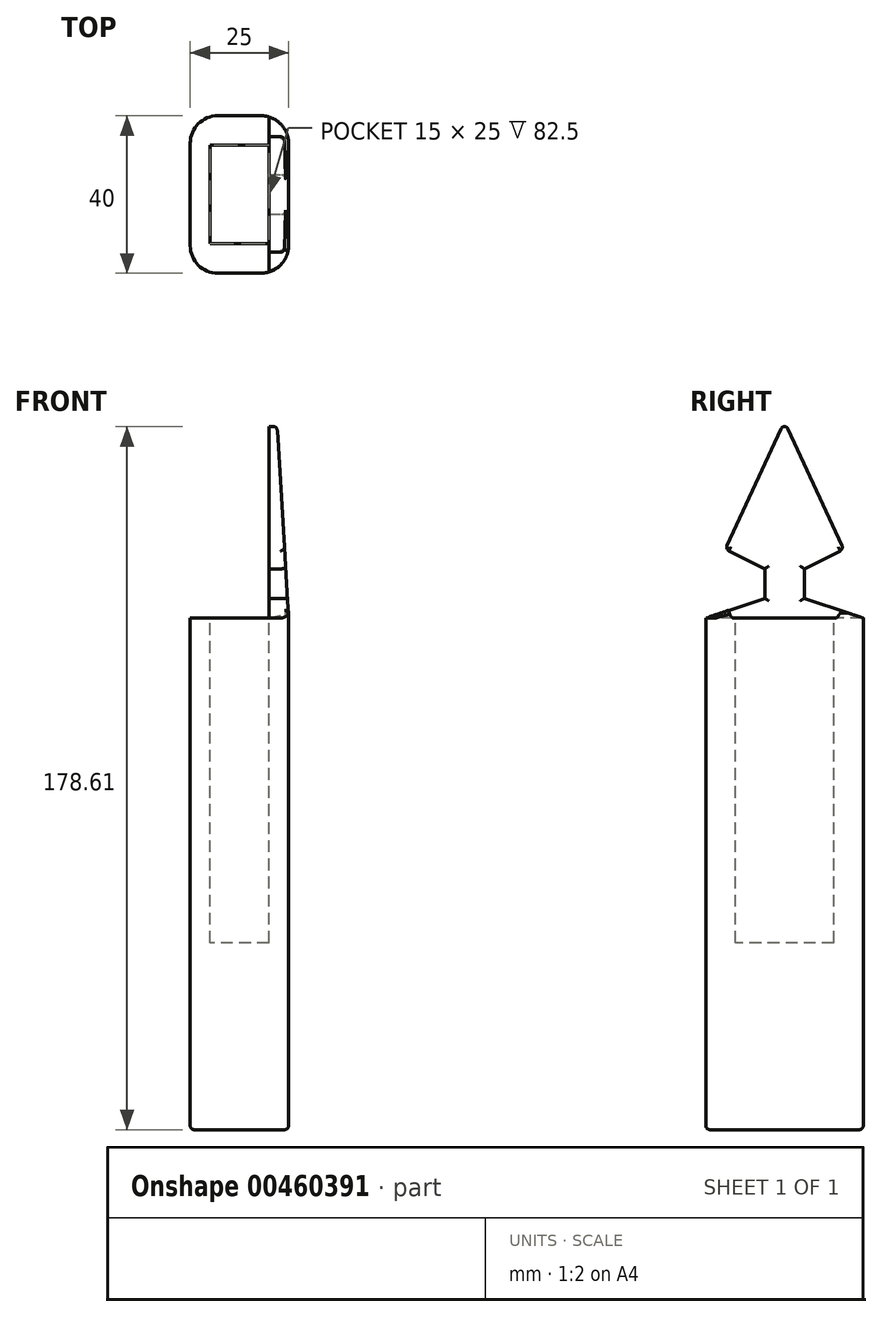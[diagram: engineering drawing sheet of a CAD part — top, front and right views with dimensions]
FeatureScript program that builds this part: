
annotation { "Feature Type Name" : "Feature", "Feature Type Description" : "" }
export const myFeature = defineFeature(function(context is Context, id is Id, definition is map)
    precondition{}
    {
        {
            var Q0;
            Q0=qCreatedBy(makeId("Top.planeOp"),FACE);
            var sketch = newSketch(context, id + "F0", { "sketchPlane" : qUnion([Q0])});
            skLineSegment(sketch, "E0.bottom", {"start": v(12.5, 20) * mm, "end": v(-12.5, 20) * mm});
            skLineSegment(sketch, "E0.top", {"start": v(12.5, -20) * mm, "end": v(-12.5, -20) * mm});
            skLineSegment(sketch, "E0.left", {"start": v(12.5, 20) * mm, "end": v(12.5, -20) * mm});
            skLineSegment(sketch, "E0.right", {"start": v(-12.5, 20) * mm, "end": v(-12.5, -20) * mm});
            skPoint(sketch, "E0.middle", {"position": v(0, 0) * mm});
            skSolve(sketch);
        }
        {
            var Q0;
            Q0=makeQuery(id+"F0.imprint","IMPRINT",FACE,{"disambiguationData":[TD([[makeQuery(id+"F0.imprint","IMPRINT",EDGE,{"derivedFrom":sQuery(id+"F0.wireOp",EDGE,"E0.bottom")}),1.0]])]});
            extrude(context, id + "F1", {"entities" : qUnion([Q0]), "endBound" : BoundingType.SYMMETRIC, "depth" : 130 * mm});
        }
        {
            var Q0;
            Q0=makeQuery(id+"F1.opExtrude","CAP_FACE",FACE,{"disambiguationData":[OSD([sQuery(id+"F0.wireOp",EDGE,"E0.bottom"),sQuery(id+"F0.wireOp",EDGE,"E0.top"),sQuery(id+"F0.wireOp",EDGE,"E0.left"),sQuery(id+"F0.wireOp",EDGE,"E0.right")])],"isStart":false});
            var sketch = newSketch(context, id + "F2", { "sketchPlane" : qUnion([Q0])});
            skLineSegment(sketch, "E1.bottom", {"start": v(7.5, 12.5) * mm, "end": v(-7.5, 12.5) * mm});
            skLineSegment(sketch, "E1.top", {"start": v(7.5, -12.5) * mm, "end": v(-7.5, -12.5) * mm});
            skLineSegment(sketch, "E1.left", {"start": v(7.5, 12.5) * mm, "end": v(7.5, -12.5) * mm});
            skLineSegment(sketch, "E1.right", {"start": v(-7.5, 12.5) * mm, "end": v(-7.5, -12.5) * mm});
            skPoint(sketch, "E1.middle", {"position": v(0, 0) * mm});
            skSolve(sketch);
        }
        {
            var Q0;
            Q0=makeQuery(id+"F2.imprint","IMPRINT",FACE,{"disambiguationData":[TD([[makeQuery(id+"F2.imprint","IMPRINT",EDGE,{"derivedFrom":sQuery(id+"F2.wireOp",EDGE,"35c8cf71-b2f7-46e8-9518-ff1371976d85.0")}),1.0]])]});
            var Q1;
            Q1=makeQuery(id+"F2.imprint","IMPRINT",FACE,{"disambiguationData":[TD([[makeQuery(id+"F2.imprint","IMPRINT",EDGE,{"derivedFrom":sQuery(id+"F2.wireOp",EDGE,"E1.bottom")}),1.0]])]});
            extrude(context, id + "F3", {"entities" : qUnion([Q0, Q1]), "operationType" : NewBodyOperationType.REMOVE, "oppositeDirection" : true, "depth" : 82.5 * mm});
        }
        {
            var Q0;
            Q0=makeQuery(id+"F1.opExtrude","SWEPT_FACE",FACE,{"disambiguationData":[OSD([sQuery(id+"F0.wireOp",EDGE,"E0.left")])]});
            var sketch = newSketch(context, id + "F4", { "sketchPlane" : qUnion([Q0])});
            skLineSegment(sketch, "E2", {"start": v(5, 70) * mm, "end": v(20, 65) * mm});
            skLineSegment(sketch, "E3", {"start": v(15, 82.5) * mm, "end": v(0, 115) * mm});
            skLineSegment(sketch, "E4.MirrorCS", {"start": v(-5, 70) * mm, "end": v(-20, 65) * mm});
            skLineSegment(sketch, "E5.MirrorCS", {"start": v(-15, 82.5) * mm, "end": v(0, 115) * mm});
            skLineSegment(sketch, "E6", {"start": v(-20, 65) * mm, "end": v(20, 65) * mm});
            skLineSegment(sketch, "E7", {"start": v(5, 70) * mm, "end": v(5, 77.5) * mm});
            skLineSegment(sketch, "E8", {"start": v(5, 77.5) * mm, "end": v(15, 82.5) * mm});
            skLineSegment(sketch, "E9.MirrorCS", {"start": v(-5, 77.5) * mm, "end": v(-15, 82.5) * mm});
            skLineSegment(sketch, "E10.MirrorCS", {"start": v(-5, 70) * mm, "end": v(-5, 77.5) * mm});
            skLineSegment(sketch, "E11", {"start": v(0, 77.5) * mm, "end": v(0, 115) * mm, "construction": true});
            skSolve(sketch);
        }
        {
            var Q0;
            Q0 = qSketchRegion(id + "F4", true);
            extrude(context, id + "F5", {"entities" : qUnion([Q0]), "operationType" : NewBodyOperationType.ADD, "oppositeDirection" : true, "depth" : 5 * mm});
        }
        {
            var Q0;
            Q0=qCreatedBy(makeId("Front.planeOp"),FACE);
            var sketch = newSketch(context, id + "F6", { "sketchPlane" : qUnion([Q0])});
            skLineSegment(sketch, "E12", {"start": v(12.5, 65) * mm, "end": v(12.5, 115) * mm});
            skLineSegment(sketch, "E13", {"start": v(12.5, 115) * mm, "end": v(9.5, 115) * mm});
            skLineSegment(sketch, "E14", {"start": v(9.5, 115) * mm, "end": v(12.5, 65) * mm});
            skLineSegment(sketch, "E15.MirrorCS", {"start": v(-9.5, 115) * mm, "end": v(-12.5, 65) * mm});
            skLineSegment(sketch, "E16.MirrorCS", {"start": v(-12.5, 115) * mm, "end": v(-9.5, 115) * mm});
            skLineSegment(sketch, "E17.MirrorCS", {"start": v(-12.5, 65) * mm, "end": v(-12.5, 115) * mm});
            skSolve(sketch);
        }
        {
            var Q0;
            Q0 = qSketchRegion(id + "F6", true);
            extrude(context, id + "F7", {"entities" : qUnion([Q0]), "operationType" : NewBodyOperationType.REMOVE, "endBound" : BoundingType.SYMMETRIC, "depth" : 50 * mm});
        }
        {
            var Q0;
            Q0=makeQuery(id+"F1.opExtrude","SWEPT_EDGE",EDGE,{"disambiguationData":[OSD([sQuery(id+"F0.wireOp",EDGE,"E0.top"),sQuery(id+"F0.wireOp",EDGE,"E0.left")])]});
            var Q1;
            Q1=makeQuery(id+"F1.opExtrude","SWEPT_EDGE",EDGE,{"disambiguationData":[OSD([sQuery(id+"F0.wireOp",EDGE,"E0.top"),sQuery(id+"F0.wireOp",EDGE,"E0.right")])]});
            var Q2;
            Q2=makeQuery(id+"F1.opExtrude","SWEPT_EDGE",EDGE,{"disambiguationData":[OSD([sQuery(id+"F0.wireOp",EDGE,"E0.bottom"),sQuery(id+"F0.wireOp",EDGE,"E0.left")])]});
            var Q3;
            Q3=makeQuery(id+"F1.opExtrude","SWEPT_EDGE",EDGE,{"disambiguationData":[OSD([sQuery(id+"F0.wireOp",EDGE,"E0.bottom"),sQuery(id+"F0.wireOp",EDGE,"E0.right")])]});
            fillet(context, id + "F8", {"entities" : qUnion([Q0, Q1, Q2, Q3]), "radius" : 7 * mm, "tangentPropagation" : true, "allowEdgeOverflow" : false});
        }
        {
            var Q0;
            Q0=makeQuery(id+"F7.boolean.opBoolean","INTERSECT",EDGE,{"derivedFrom":[makeQuery(id+"F5.opExtrude","SWEPT_FACE",FACE,{"disambiguationData":[OSD([sQuery(id+"F4.wireOp",EDGE,"E5.MirrorCS")])]}),makeQuery(id+"F7.opExtrude","SWEPT_FACE",FACE,{"disambiguationData":[OSD([sQuery(id+"F6.wireOp",EDGE,"E14")])]})]});
            var Q1;
            Q1=makeQuery(id+"F7.boolean.opBoolean","INTERSECT",EDGE,{"derivedFrom":[makeQuery(id+"F5.opExtrude","SWEPT_FACE",FACE,{"disambiguationData":[OSD([sQuery(id+"F4.wireOp",EDGE,"E3")])]}),makeQuery(id+"F7.opExtrude","SWEPT_FACE",FACE,{"disambiguationData":[OSD([sQuery(id+"F6.wireOp",EDGE,"E14")])]})]});
            var Q2;
            Q2=makeQuery(id+"F7.boolean.opBoolean","INTERSECT",EDGE,{"derivedFrom":[makeQuery(id+"FizvMhToMbJq8fq_1.1.F5.opExtrude","SWEPT_FACE",FACE,{"disambiguationData":[OSD([sQuery(id+"F4.wireOp",EDGE,"E5.MirrorCS")])]}),makeQuery(id+"F7.opExtrude","SWEPT_FACE",FACE,{"disambiguationData":[OSD([sQuery(id+"F6.wireOp",EDGE,"E15.MirrorCS")])]})]});
            var Q3;
            Q3=makeQuery(id+"F7.boolean.opBoolean","INTERSECT",EDGE,{"derivedFrom":[makeQuery(id+"FizvMhToMbJq8fq_1.1.F5.opExtrude","SWEPT_FACE",FACE,{"disambiguationData":[OSD([sQuery(id+"F4.wireOp",EDGE,"E3")])]}),makeQuery(id+"F7.opExtrude","SWEPT_FACE",FACE,{"disambiguationData":[OSD([sQuery(id+"F6.wireOp",EDGE,"E15.MirrorCS")])]})]});
            var Q4;
            Q4=makeQuery(id+"F7.boolean.opBoolean","INTERSECT",EDGE,{"derivedFrom":[makeQuery(id+"F5.opExtrude","SWEPT_FACE",FACE,{"disambiguationData":[OSD([sQuery(id+"F4.wireOp",EDGE,"E9.MirrorCS")])]}),makeQuery(id+"F7.opExtrude","SWEPT_FACE",FACE,{"disambiguationData":[OSD([sQuery(id+"F6.wireOp",EDGE,"E14")])]})]});
            var Q5;
            Q5=makeQuery(id+"F5.opExtrude","SWEPT_EDGE",EDGE,{"disambiguationData":[OSD([sQuery(id+"F4.wireOp",EDGE,"E5.MirrorCS"),sQuery(id+"F4.wireOp",EDGE,"E9.MirrorCS")])]});
            var Q6;
            Q6=makeQuery(id+"F7.boolean.opBoolean","INTERSECT",EDGE,{"derivedFrom":[makeQuery(id+"F5.opExtrude","SWEPT_FACE",FACE,{"disambiguationData":[OSD([sQuery(id+"F4.wireOp",EDGE,"E10.MirrorCS")])]}),makeQuery(id+"F7.opExtrude","SWEPT_FACE",FACE,{"disambiguationData":[OSD([sQuery(id+"F6.wireOp",EDGE,"E14")])]})]});
            var Q7;
            Q7=makeQuery(id+"F7.boolean.opBoolean","INTERSECT",EDGE,{"derivedFrom":[makeQuery(id+"F5.opExtrude","SWEPT_FACE",FACE,{"disambiguationData":[OSD([sQuery(id+"F4.wireOp",EDGE,"E4.MirrorCS")])]}),makeQuery(id+"F7.opExtrude","SWEPT_FACE",FACE,{"disambiguationData":[OSD([sQuery(id+"F6.wireOp",EDGE,"E14")])]})]});
            var Q8;
            Q8=makeQuery(id+"F8.opFillet","BLEND_EDGE",EDGE,{"blendedFrom":[makeQuery(id+"F1.opExtrude","SWEPT_EDGE",EDGE,{"disambiguationData":[OSD([sQuery(id+"F0.wireOp",EDGE,"E0.top"),sQuery(id+"F0.wireOp",EDGE,"E0.left")])]}),makeQuery(id+"F5.opExtrude","SWEPT_FACE",FACE,{"disambiguationData":[OSD([sQuery(id+"F4.wireOp",EDGE,"E4.MirrorCS")])]})],"blendedInto":[makeQuery(id+"F5.opExtrude","SWEPT_FACE",FACE,{"disambiguationData":[OSD([sQuery(id+"F4.wireOp",EDGE,"E4.MirrorCS")])]})]});
            var Q9;
            Q9=makeQuery(id+"F8.opFillet","BLEND_EDGE",EDGE,{"blendedFrom":[makeQuery(id+"F1.opExtrude","SWEPT_EDGE",EDGE,{"disambiguationData":[OSD([sQuery(id+"F0.wireOp",EDGE,"E0.top"),sQuery(id+"F0.wireOp",EDGE,"E0.right")])]}),makeQuery(id+"FizvMhToMbJq8fq_1.1.F5.opExtrude","SWEPT_FACE",FACE,{"disambiguationData":[OSD([sQuery(id+"F4.wireOp",EDGE,"E4.MirrorCS")])]})],"blendedInto":[makeQuery(id+"FizvMhToMbJq8fq_1.1.F5.opExtrude","SWEPT_FACE",FACE,{"disambiguationData":[OSD([sQuery(id+"F4.wireOp",EDGE,"E4.MirrorCS")])]})]});
            var Q10;
            Q10=makeQuery(id+"F7.boolean.opBoolean","INTERSECT",EDGE,{"derivedFrom":[makeQuery(id+"FizvMhToMbJq8fq_1.1.F5.opExtrude","SWEPT_FACE",FACE,{"disambiguationData":[OSD([sQuery(id+"F4.wireOp",EDGE,"E4.MirrorCS")])]}),makeQuery(id+"F7.opExtrude","SWEPT_FACE",FACE,{"disambiguationData":[OSD([sQuery(id+"F6.wireOp",EDGE,"E15.MirrorCS")])]})]});
            var Q11;
            Q11=makeQuery(id+"F7.boolean.opBoolean","INTERSECT",EDGE,{"derivedFrom":[makeQuery(id+"FizvMhToMbJq8fq_1.1.F5.opExtrude","SWEPT_FACE",FACE,{"disambiguationData":[OSD([sQuery(id+"F4.wireOp",EDGE,"E10.MirrorCS")])]}),makeQuery(id+"F7.opExtrude","SWEPT_FACE",FACE,{"disambiguationData":[OSD([sQuery(id+"F6.wireOp",EDGE,"E15.MirrorCS")])]})]});
            var Q12;
            Q12=makeQuery(id+"F7.boolean.opBoolean","INTERSECT",EDGE,{"derivedFrom":[makeQuery(id+"FizvMhToMbJq8fq_1.1.F5.opExtrude","SWEPT_FACE",FACE,{"disambiguationData":[OSD([sQuery(id+"F4.wireOp",EDGE,"E9.MirrorCS")])]}),makeQuery(id+"F7.opExtrude","SWEPT_FACE",FACE,{"disambiguationData":[OSD([sQuery(id+"F6.wireOp",EDGE,"E15.MirrorCS")])]})]});
            var Q13;
            Q13=makeQuery(id+"F7.boolean.opBoolean","INTERSECT",EDGE,{"derivedFrom":[makeQuery(id+"FizvMhToMbJq8fq_1.1.F5.opExtrude","SWEPT_FACE",FACE,{"disambiguationData":[OSD([sQuery(id+"F4.wireOp",EDGE,"E8")])]}),makeQuery(id+"F7.opExtrude","SWEPT_FACE",FACE,{"disambiguationData":[OSD([sQuery(id+"F6.wireOp",EDGE,"E15.MirrorCS")])]})]});
            var Q14;
            Q14=makeQuery(id+"F7.boolean.opBoolean","INTERSECT",EDGE,{"derivedFrom":[makeQuery(id+"FizvMhToMbJq8fq_1.1.F5.opExtrude","SWEPT_FACE",FACE,{"disambiguationData":[OSD([sQuery(id+"F4.wireOp",EDGE,"E7")])]}),makeQuery(id+"F7.opExtrude","SWEPT_FACE",FACE,{"disambiguationData":[OSD([sQuery(id+"F6.wireOp",EDGE,"E15.MirrorCS")])]})]});
            var Q15;
            Q15=makeQuery(id+"F7.boolean.opBoolean","INTERSECT",EDGE,{"derivedFrom":[makeQuery(id+"FizvMhToMbJq8fq_1.1.F5.opExtrude","SWEPT_FACE",FACE,{"disambiguationData":[OSD([sQuery(id+"F4.wireOp",EDGE,"E2")])]}),makeQuery(id+"F7.opExtrude","SWEPT_FACE",FACE,{"disambiguationData":[OSD([sQuery(id+"F6.wireOp",EDGE,"E15.MirrorCS")])]})]});
            var Q16;
            Q16=makeQuery(id+"F8.opFillet","BLEND_EDGE",EDGE,{"blendedFrom":[makeQuery(id+"F1.opExtrude","SWEPT_EDGE",EDGE,{"disambiguationData":[OSD([sQuery(id+"F0.wireOp",EDGE,"E0.bottom"),sQuery(id+"F0.wireOp",EDGE,"E0.right")])]}),makeQuery(id+"FizvMhToMbJq8fq_1.1.F5.opExtrude","SWEPT_FACE",FACE,{"disambiguationData":[OSD([sQuery(id+"F4.wireOp",EDGE,"E2")])]})],"blendedInto":[makeQuery(id+"FizvMhToMbJq8fq_1.1.F5.opExtrude","SWEPT_FACE",FACE,{"disambiguationData":[OSD([sQuery(id+"F4.wireOp",EDGE,"E2")])]})]});
            var Q17;
            Q17=makeQuery(id+"F7.boolean.opBoolean","INTERSECT",EDGE,{"derivedFrom":[makeQuery(id+"F5.opExtrude","SWEPT_FACE",FACE,{"disambiguationData":[OSD([sQuery(id+"F4.wireOp",EDGE,"E7")])]}),makeQuery(id+"F7.opExtrude","SWEPT_FACE",FACE,{"disambiguationData":[OSD([sQuery(id+"F6.wireOp",EDGE,"E14")])]})]});
            var Q18;
            Q18=makeQuery(id+"F7.boolean.opBoolean","INTERSECT",EDGE,{"derivedFrom":[makeQuery(id+"F5.opExtrude","SWEPT_FACE",FACE,{"disambiguationData":[OSD([sQuery(id+"F4.wireOp",EDGE,"E8")])]}),makeQuery(id+"F7.opExtrude","SWEPT_FACE",FACE,{"disambiguationData":[OSD([sQuery(id+"F6.wireOp",EDGE,"E14")])]})]});
            var Q19;
            Q19=makeQuery(id+"F7.boolean.opBoolean","INTERSECT",EDGE,{"derivedFrom":[makeQuery(id+"F5.opExtrude","SWEPT_FACE",FACE,{"disambiguationData":[OSD([sQuery(id+"F4.wireOp",EDGE,"E2")])]}),makeQuery(id+"F7.opExtrude","SWEPT_FACE",FACE,{"disambiguationData":[OSD([sQuery(id+"F6.wireOp",EDGE,"E14")])]})]});
            var Q20;
            Q20=makeQuery(id+"F5.opExtrude","SWEPT_EDGE",EDGE,{"disambiguationData":[OSD([sQuery(id+"F4.wireOp",EDGE,"E3"),sQuery(id+"F4.wireOp",EDGE,"E8")])]});
            var Q21;
            Q21=makeQuery(id+"FizvMhToMbJq8fq_1.1.F5.opExtrude","SWEPT_EDGE",EDGE,{"disambiguationData":[OSD([sQuery(id+"F4.wireOp",EDGE,"E3"),sQuery(id+"F4.wireOp",EDGE,"E8")])]});
            var Q22;
            Q22=makeQuery(id+"FizvMhToMbJq8fq_1.1.F5.opExtrude","SWEPT_EDGE",EDGE,{"disambiguationData":[OSD([sQuery(id+"F4.wireOp",EDGE,"E3"),sQuery(id+"F4.wireOp",EDGE,"E5.MirrorCS")])]});
            var Q23;
            Q23=makeQuery(id+"F5.opExtrude","SWEPT_EDGE",EDGE,{"disambiguationData":[OSD([sQuery(id+"F4.wireOp",EDGE,"E3"),sQuery(id+"F4.wireOp",EDGE,"E5.MirrorCS")])]});
            var Q24;
            Q24=makeQuery(id+"FizvMhToMbJq8fq_1.1.F5.opExtrude","SWEPT_EDGE",EDGE,{"disambiguationData":[OSD([sQuery(id+"F4.wireOp",EDGE,"E5.MirrorCS"),sQuery(id+"F4.wireOp",EDGE,"E9.MirrorCS")])]});
            var Q25;
            Q25=makeQuery(id+"F1.opExtrude","CAP_EDGE",EDGE,{"disambiguationData":[OSD([sQuery(id+"F0.wireOp",EDGE,"E0.bottom")])],"isStart":true});
            fillet(context, id + "F9", {"entities" : qUnion([Q0, Q1, Q2, Q3, Q4, Q5, Q6, Q7, Q8, Q9, Q10, Q11, Q12, Q13, Q14, Q15, Q16, Q17, Q18, Q19, Q20, Q21, Q22, Q23, Q24, Q25]), "radius" : 1 * mm, "tangentPropagation" : true, "allowEdgeOverflow" : false});
        }
    });
